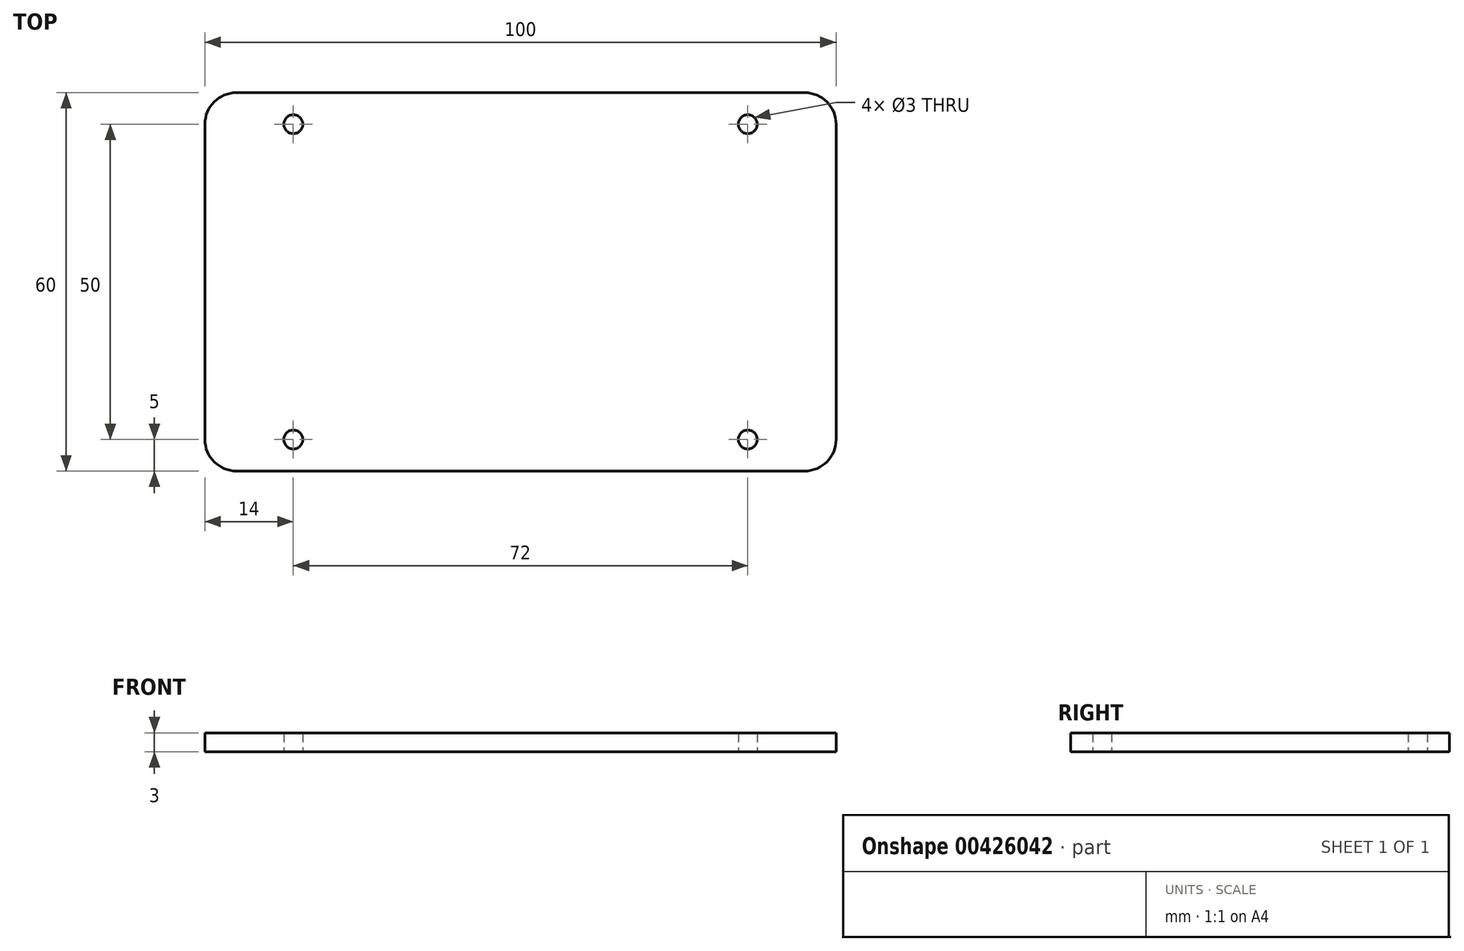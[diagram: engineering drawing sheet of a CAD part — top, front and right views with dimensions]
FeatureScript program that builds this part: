
annotation { "Feature Type Name" : "Feature", "Feature Type Description" : "" }
export const myFeature = defineFeature(function(context is Context, id is Id, definition is map)
    precondition{}
    {
        {
            var Q0;
            Q0=qCreatedBy(makeId("Top.planeOp"),FACE);
            var sketch = newSketch(context, id + "F0", { "sketchPlane" : qUnion([Q0])});
            skLineSegment(sketch, "E0.bottom", {"start": v(45, -30) * mm, "end": v(-45, -30) * mm});
            skLineSegment(sketch, "E0.top", {"start": v(45, 30) * mm, "end": v(-45, 30) * mm});
            skLineSegment(sketch, "E0.left", {"start": v(50, -25) * mm, "end": v(50, 25) * mm});
            skLineSegment(sketch, "E0.right", {"start": v(-50, -25) * mm, "end": v(-50, 25) * mm});
            skPoint(sketch, "E0.middle", {"position": v(0, 0) * mm});
            skCircle(sketch, "E1", {"center": v(-36, 25) * mm, "radius": 1.5 * mm});
            skCircle(sketch, "E2.MirrorC", {"center": v(36, 25) * mm, "radius": 1.5 * mm});
            skCircle(sketch, "E3.MirrorC", {"center": v(-36, -25) * mm, "radius": 1.5 * mm});
            skCircle(sketch, "E4.MirrorC", {"center": v(36, -25) * mm, "radius": 1.5 * mm});
            skPoint(sketch, "E5.visualSharp", {"position": v(-50, 30) * mm});
            skArc(sketch, "E5.filletArc", {"start": v(-45, 30) * mm, "mid": v(-48.54, 28.54) * mm, "end": v(-50, 25) * mm});
            skPoint(sketch, "E6.visualSharp", {"position": v(-50, -30) * mm});
            skArc(sketch, "E6.filletArc", {"start": v(-50, -25) * mm, "mid": v(-48.54, -28.54) * mm, "end": v(-45, -30) * mm});
            skPoint(sketch, "E7.visualSharp", {"position": v(50, -30) * mm});
            skArc(sketch, "E7.filletArc", {"start": v(45, -30) * mm, "mid": v(48.54, -28.54) * mm, "end": v(50, -25) * mm});
            skPoint(sketch, "E8.visualSharp", {"position": v(50, 30) * mm});
            skArc(sketch, "E8.filletArc", {"start": v(50, 25) * mm, "mid": v(48.54, 28.54) * mm, "end": v(45, 30) * mm});
            skSolve(sketch);
        }
        {
            var Q0;
            Q0=makeQuery(id+"F0.imprint","IMPRINT",FACE,{"disambiguationData":[TD([[makeQuery(id+"F0.imprint","IMPRINT",EDGE,{"derivedFrom":sQuery(id+"F0.wireOp",EDGE,"E0.bottom")}),-1.0]])]});
            extrude(context, id + "F1", {"entities" : qUnion([Q0]), "depth" : 3 * mm});
        }
    });
